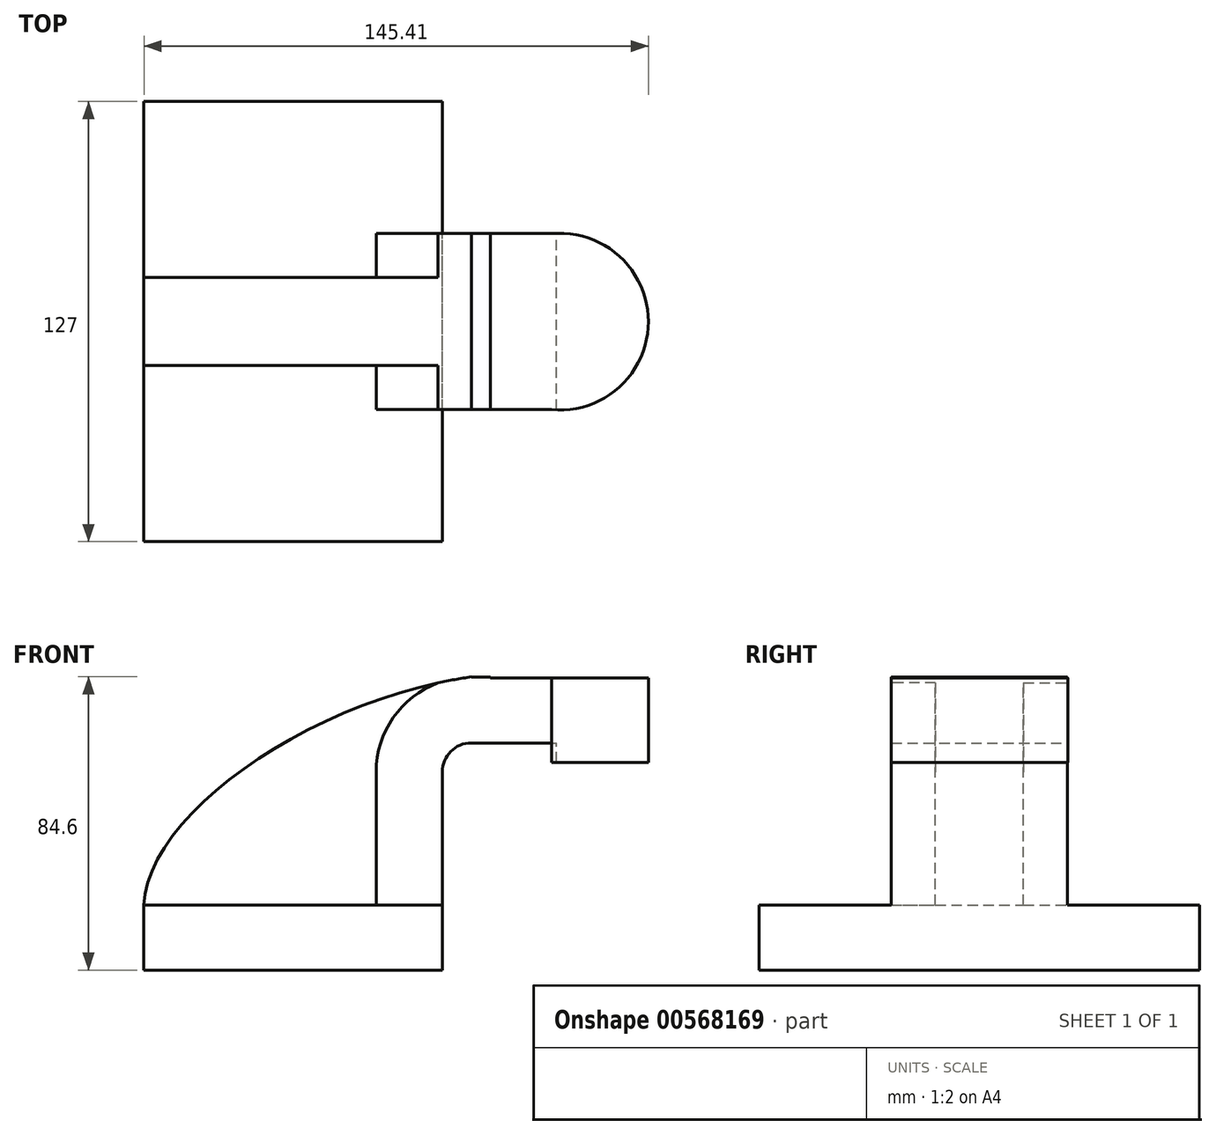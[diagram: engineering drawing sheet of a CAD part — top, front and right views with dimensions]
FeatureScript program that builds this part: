
annotation { "Feature Type Name" : "Feature", "Feature Type Description" : "" }
export const myFeature = defineFeature(function(context is Context, id is Id, definition is map)
    precondition{}
    {
        {
            var Q0;
            Q0=qCreatedBy(makeId("Front.planeOp"),FACE);
            var sketch = newSketch(context, id + "F0", { "sketchPlane" : qUnion([Q0])});
            skLineSegment(sketch, "E0.bottom", {"start": v(43, 9.37) * mm, "end": v(-43, 9.37) * mm});
            skLineSegment(sketch, "E0.top", {"start": v(43, -9.37) * mm, "end": v(-43, -9.37) * mm});
            skLineSegment(sketch, "E0.left", {"start": v(43, 9.37) * mm, "end": v(43, -9.37) * mm});
            skLineSegment(sketch, "E0.right", {"start": v(-43, 9.37) * mm, "end": v(-43, -9.37) * mm});
            skPoint(sketch, "E0.middle", {"position": v(0, 0) * mm});
            skLineSegment(sketch, "E1.bottom", {"start": v(56.82, 50.22) * mm, "end": v(95.53, 50.22) * mm});
            skLineSegment(sketch, "E1.top", {"start": v(56.82, 80.32) * mm, "end": v(95.53, 80.32) * mm});
            skLineSegment(sketch, "E1.left", {"start": v(56.82, 50.22) * mm, "end": v(56.82, 80.32) * mm});
            skLineSegment(sketch, "E1.right", {"start": v(95.53, 50.22) * mm, "end": v(95.53, 80.32) * mm});
            skPoint(sketch, "E1.middle", {"position": v(76.18, 65.27) * mm});
            skLineSegment(sketch, "E2", {"start": v(43, 9.37) * mm, "end": v(43, 47.76) * mm});
            skArc(sketch, "E3", {"start": v(43, 47.76) * mm, "mid": v(45.47, 53.71) * mm, "end": v(51.42, 56.18) * mm});
            skLineSegment(sketch, "E4", {"start": v(51.42, 56.18) * mm, "end": v(76.18, 56.18) * mm});
            skLineSegment(sketch, "E5.0", {"start": v(51.42, 75.23) * mm, "end": v(76.18, 75.23) * mm});
            skArc(sketch, "E5.1", {"start": v(23.95, 47.76) * mm, "mid": v(32, 67.18) * mm, "end": v(51.42, 75.23) * mm});
            skLineSegment(sketch, "E5.2", {"start": v(23.95, 9.37) * mm, "end": v(23.95, 47.76) * mm});
            skFitSpline(sketch, "E6", {"points": [v(-43, 9.37) * mm, v(51.42, 75.23) * mm], "startDerivative": vector(2.76, 79.25) * mm, "endDerivative": vector(138.58, 19.73) * mm});
            skSolve(sketch);
        }
        {
            var Q0;
            Q0=makeQuery(id+"F0.imprint","IMPRINT",FACE,{"disambiguationData":[TD([[makeQuery(id+"F0.imprint","IMPRINT",EDGE,{"derivedFrom":sQuery(id+"F0.wireOp",EDGE,"E0.top")}),-1.0]])]});
            extrude(context, id + "F1", {"entities" : qUnion([Q0]), "endBound" : BoundingType.SYMMETRIC, "depth" : 127 * mm, "offsetDistance" : 25.4 * mm});
        }
        {
            var Q0;
            {var subQ1=sQuery(id+"F0.wireOp",EDGE,"E2");Q0=makeQuery(id+"F0.imprint","IMPRINT",FACE,{"disambiguationData":[TD([[makeQuery(id+"F0.imprint","IMPRINT",EDGE,{"derivedFrom":subQ1}),1.0]])]});}
            extrude(context, id + "F2", {"entities" : qUnion([Q0]), "operationType" : NewBodyOperationType.ADD, "endBound" : BoundingType.SYMMETRIC, "depth" : 50.8 * mm, "offsetDistance" : 25.4 * mm});
        }
        {
            var Q0;
            {var subQ3=sQuery(id+"F0.wireOp",EDGE,"E5.2");Q0=makeQuery(id+"F0.imprint","IMPRINT",FACE,{"disambiguationData":[TD([[makeQuery(id+"F0.imprint","IMPRINT",EDGE,{"derivedFrom":subQ3}),1.0]])]});}
            extrude(context, id + "F3", {"entities" : qUnion([Q0]), "operationType" : NewBodyOperationType.ADD, "endBound" : BoundingType.SYMMETRIC, "depth" : 25.4 * mm, "offsetDistance" : 25.4 * mm});
        }
        {
            var Q0;
            Q0=qCreatedBy(makeId("Front.planeOp"),FACE);
            var sketch = newSketch(context, id + "F4", { "sketchPlane" : qUnion([Q0])});
            skLineSegment(sketch, "E7.bottom", {"start": v(56.78, 74.9) * mm, "end": v(75.96, 74.9) * mm});
            skLineSegment(sketch, "E7.top", {"start": v(56.78, 56.14) * mm, "end": v(75.96, 56.14) * mm});
            skLineSegment(sketch, "E7.left", {"start": v(56.78, 74.9) * mm, "end": v(56.78, 56.14) * mm});
            skLineSegment(sketch, "E7.right", {"start": v(75.96, 74.9) * mm, "end": v(75.96, 56.14) * mm});
            skSolve(sketch);
        }
        {
            var Q0;
            Q0 = qSketchRegion(id + "F4", true);
            extrude(context, id + "F5", {"entities" : qUnion([Q0]), "operationType" : NewBodyOperationType.ADD, "endBound" : BoundingType.SYMMETRIC, "depth" : 50.8 * mm, "offsetDistance" : 25.4 * mm});
        }
        {
            var Q0;
            Q0=makeQuery(id+"F5.opExtrude","SWEPT_FACE",FACE,{"disambiguationData":[OSD([sQuery(id+"F4.wireOp",EDGE,"E7.bottom")])]});
            var sketch = newSketch(context, id + "F6", { "sketchPlane" : qUnion([Q0])});
            skCircle(sketch, "E8", {"center": v(76.29, 0) * mm, "radius": 25.6 * mm});
            skSolve(sketch);
        }
        {
            var Q0;
            {var subQ0=sQuery(id+"F4.wireOp",EDGE,"E7.bottom");var subQ2=makeQuery(id+"F5.opExtrude","SWEPT_EDGE",EDGE,{"disambiguationData":[OSD([subQ0,sQuery(id+"F4.wireOp",EDGE,"E7.right")])]});Q0=makeQuery(id+"F6.imprint","IMPRINT",FACE,{"disambiguationData":[TD([[makeQuery(id+"F6.imprint","IMPRINT",EDGE,{"derivedFrom":subQ2}),1.0]])]});}
            var sketch = newSketch(context, id + "F7", { "sketchPlane" : qUnion([Q0])});
            skCircle(sketch, "E9", {"center": v(76.9, 0) * mm, "radius": 25.5 * mm});
            skSolve(sketch);
        }
        {
            var Q0;
            {var subQ1=sQuery(id+"F4.wireOp",EDGE,"E7.bottom");var subQ3=makeQuery(id+"F5.opExtrude","SWEPT_EDGE",EDGE,{"disambiguationData":[OSD([subQ1,sQuery(id+"F4.wireOp",EDGE,"E7.right")])]});var subQ10=makeQuery(id+"F6.imprint","IMPRINT",EDGE,{"derivedFrom":subQ3});Q0=makeQuery(id+"F7.imprint","IMPRINT",FACE,{"disambiguationData":[TD([[makeQuery(id+"F7.imprint","IMPRINT",EDGE,{"derivedFrom":subQ10}),-1.0]])]});}
            extrude(context, id + "F8", {"entities" : qUnion([Q0]), "operationType" : NewBodyOperationType.ADD, "oppositeDirection" : true, "depth" : 24.38 * mm, "offsetDistance" : 25.4 * mm});
        }
    });
